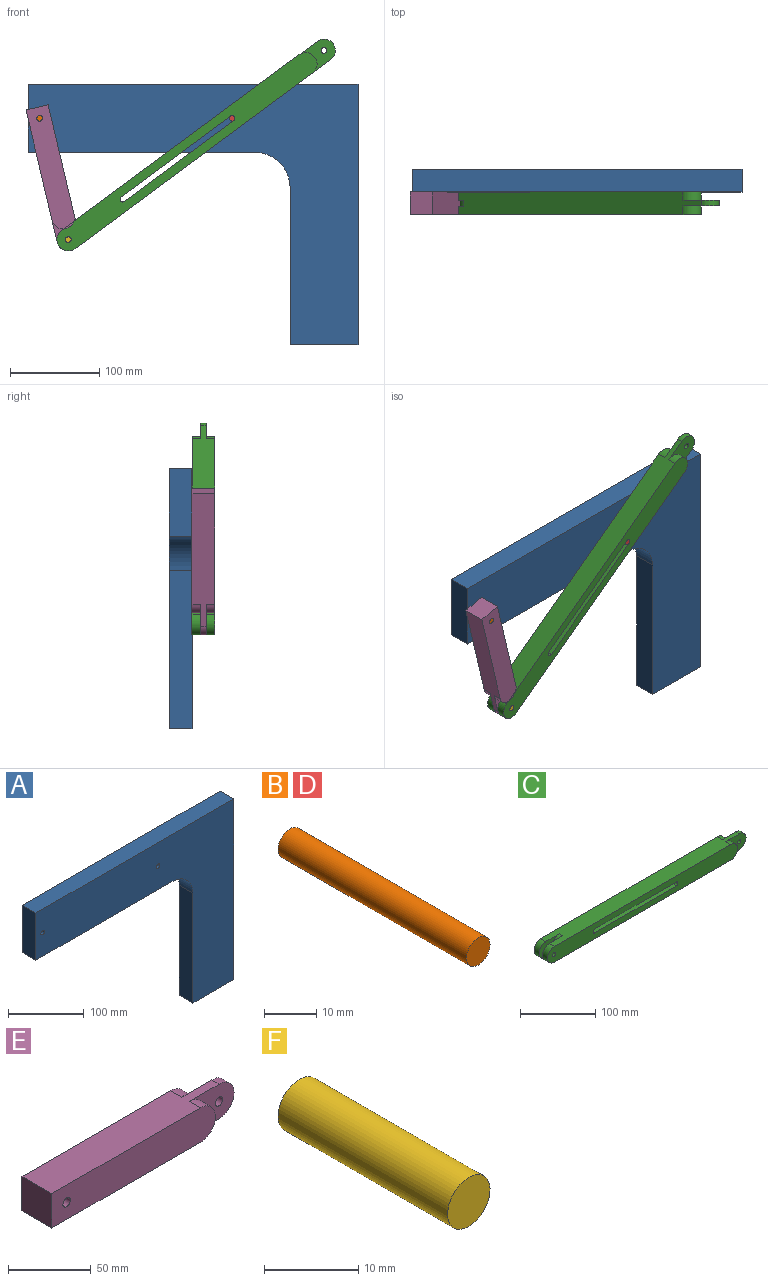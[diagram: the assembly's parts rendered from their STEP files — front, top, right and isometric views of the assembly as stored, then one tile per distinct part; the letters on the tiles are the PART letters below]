
ASSEMBLY  parts=6 mates=6
PART A: 11 faces, bbox 369.7x25.4x292.1 mm
  f0: plane 292.1x25.4mm, normal (1,0,0), area 7419.3mm2, adj f1,f7,f9,f10
  f1: plane 369.7x25.4mm, normal (0,0,1), area 9390.4mm2, adj f0,f2,f9,f10
  f2: plane 76.2x25.4mm, normal (-1,0,0), area 1935.5mm2, adj f1,f3,f9,f10
  f3: plane 254x25.4mm, normal (0,0,-1), area 6451.6mm2, adj f2,f4,f9,f10
  f4: cylinder r=39.53mm len=39.5mm, axis (0,-1,0), area 1540.8mm2, adj f3,f5,f9,f10
  f5: plane 177.8x25.4mm, normal (-1,0,0), area 4516.1mm2, adj f4,f7,f9,f10
  f6: cylinder r=3.17mm len=25.4mm, axis (0,-1,0), area 506.7mm2, adj f9,f10
  f7: plane 76.2x25.4mm, normal (0,0,-1), area 1935.5mm2, adj f0,f5,f9,f10
  f8: cylinder r=3.17mm len=25.4mm, axis (0,-1,0), area 506.7mm2, adj f9,f10
  f9: plane 369.7x292.1mm, normal (0,1,0), area 44893.8mm2, adj f0,f1,f2,f3,f4,f5,f6,f7
  f10: plane 369.7x292.1mm, normal (0,-1,0), area 44893.8mm2, adj f0,f1,f2,f3,f4,f5,f6,f7
PART B: 3 faces, bbox 6.4x50.8x6.4 mm
  f0: cylinder r=3.17mm len=50.8mm, axis (0,-1,0), area 1013.4mm2, adj f1,f2
  f1: plane 6.35x6.35mm, normal (0,1,0), area 31.7mm2, adj f0
  f2: plane 6.35x6.35mm, normal (0,-1,0), area 31.7mm2, adj f0
PART C: 21 faces, bbox 382x25.4x25.4 mm
  f0: plane 356.62x25.4mm, normal (0,0,1), area 8412.9mm2, adj f1,f3,f8,f11,f12,f13,f14,f15
  f1: cylinder r=12.7mm len=25.4mm, axis (0,-1,0), area 380mm2, adj f0,f2,f11,f14
  f2: plane 356.62x25.4mm, normal (0,0,-1), area 8412.9mm2, adj f1,f3,f8,f11,f12,f13,f14,f15
  f3: cylinder r=12.7mm len=25.4mm, axis (0,-1,0), area 253.4mm2, adj f0,f2,f15,f16
  f4: cylinder r=3.17mm len=9.53mm, axis (0,-1,0), area 190mm2, adj f11,f14
  f5: cylinder r=3.17mm len=25.4mm, axis (0,-1,0), area 253.4mm2, adj f6,f10,f11,f12
  f6: plane 152.4x25.4mm, normal (0,0,-1), area 3871mm2, adj f5,f7,f11,f12
  f7: cylinder r=3.17mm len=25.4mm, axis (0,-1,0), area 253.4mm2, adj f6,f10,f11,f12
  f8: cylinder r=12.7mm len=25.4mm, axis (0,-1,0), area 380mm2, adj f0,f2,f12,f13
  f9: cylinder r=3.17mm len=9.53mm, axis (0,-1,0), area 190mm2, adj f12,f13
  f10: plane 152.4x25.4mm, normal (0,0,1), area 3871mm2, adj f5,f7,f11,f12
  f11: plane 356.62x25.4mm, normal (0,1,0), area 7888.5mm2, adj f0,f1,f2,f4,f5,f6,f7,f10
  f12: plane 356.62x25.4mm, normal (0,-1,0), area 7888.5mm2, adj f0,f2,f5,f6,f7,f8,f9,f10
  f13: plane 38.1x25.4mm, normal (0,1,0), area 613.5mm2, adj f0,f2,f8,f9,f20
  f14: plane 38.1x25.4mm, normal (0,-1,0), area 613.5mm2, adj f0,f1,f2,f4,f20
  f15: plane 38.1x25.4mm, normal (0,1,0), area 613.5mm2, adj f0,f2,f3,f17,f18
  f16: plane 38.1x25.4mm, normal (0,-1,0), area 613.5mm2, adj f0,f2,f3,f17,f19
  f17: cylinder r=3.17mm len=6.35mm, axis (0,-1,0), area 126.7mm2, adj f15,f16
  f18: cylinder r=12.7mm len=25.4mm, axis (0,1,0), area 380mm2, adj f0,f2,f11,f15
  f19: cylinder r=12.7mm len=25.4mm, axis (0,1,0), area 380mm2, adj f0,f2,f12,f16
  f20: cylinder r=12.7mm len=25.4mm, axis (0,-1,0), area 253.4mm2, adj f0,f2,f13,f14
PART D: same geometry as B
PART E: 12 faces, bbox 165.1x25.4x25.4 mm
  f0: cylinder r=12.7mm len=25.4mm, axis (0,-1,0), area 253.4mm2, adj f3,f4,f7,f8
  f1: plane 139.7x25.4mm, normal (0,1,0), area 3447.5mm2, adj f3,f4,f5,f6,f11
  f2: plane 139.7x25.4mm, normal (0,-1,0), area 3447.5mm2, adj f3,f4,f5,f6,f10
  f3: plane 152.4x25.4mm, normal (0,0,-1), area 3387.1mm2, adj f0,f1,f2,f5,f7,f8,f10,f11
  f4: plane 152.4x25.4mm, normal (0,0,1), area 3387.1mm2, adj f0,f1,f2,f5,f7,f8,f10,f11
  f5: plane 25.4x25.4mm, normal (-1,0,0), area 645.2mm2, adj f1,f2,f3,f4
  f6: cylinder r=3.17mm len=25.4mm, axis (0,-1,0), area 506.7mm2, adj f1,f2
  f7: plane 38.1x25.4mm, normal (0,-1,0), area 613.5mm2, adj f0,f3,f4,f9,f10
  f8: plane 38.1x25.4mm, normal (0,1,0), area 613.5mm2, adj f0,f3,f4,f9,f11
  f9: cylinder r=3.17mm len=6.35mm, axis (0,-1,0), area 126.7mm2, adj f7,f8
  f10: cylinder r=12.7mm len=25.4mm, axis (0,1,0), area 380mm2, adj f2,f3,f4,f7
  f11: cylinder r=12.7mm len=25.4mm, axis (0,1,0), area 380mm2, adj f1,f3,f4,f8
PART F: 3 faces, bbox 6.4x25.4x6.4 mm
  f0: cylinder r=3.17mm len=25.4mm, axis (0,-1,0), area 506.7mm2, adj f1,f2
  f1: plane 6.35x6.35mm, normal (0,1,0), area 31.7mm2, adj f0
  f2: plane 6.35x6.35mm, normal (0,-1,0), area 31.7mm2, adj f0
PLACE A t=(-137.91,-213.76,152.91)mm fixed
PLACE B t=(-444.93,-213.76,-75.35)mm
PLACE C rot(axis=(0,-1,0),36.5deg) t=(-66.86,-239.16,-88.66)mm
PLACE D t=(-229.03,-213.76,-75.35)mm
PLACE E rot(axis=(0,1,0),76.7deg) t=(-279.29,-239.16,-110.05)mm
PLACE F rot(axis=(0,-1,0),4.4deg) t=(-380.12,-239.16,-227.77)mm
MATE revolute F.f0 <-> E.f0  axis (0,-1,0) through (-204.68,-226.46,-187.72)mm
MATE fastened D.f0 <-> A.f6  axis (0,1,0) through (-20.9,-188.36,-51.77)mm
MATE pin_slot D.f0 <-> C.f12  axis (0,-1,0) through (-20.9,-239.16,-51.77)mm
MATE revolute E.f6 <-> B.f0  axis (0,-1,0) through (-236.8,-239.16,-51.77)mm
MATE revolute C.f1 <-> F.f0  axis (0,-1,0) through (-204.68,-239.16,-187.72)mm
MATE fastened B.f0 <-> A.f8  axis (0,1,0) through (-236.8,-188.36,-51.77)mm
